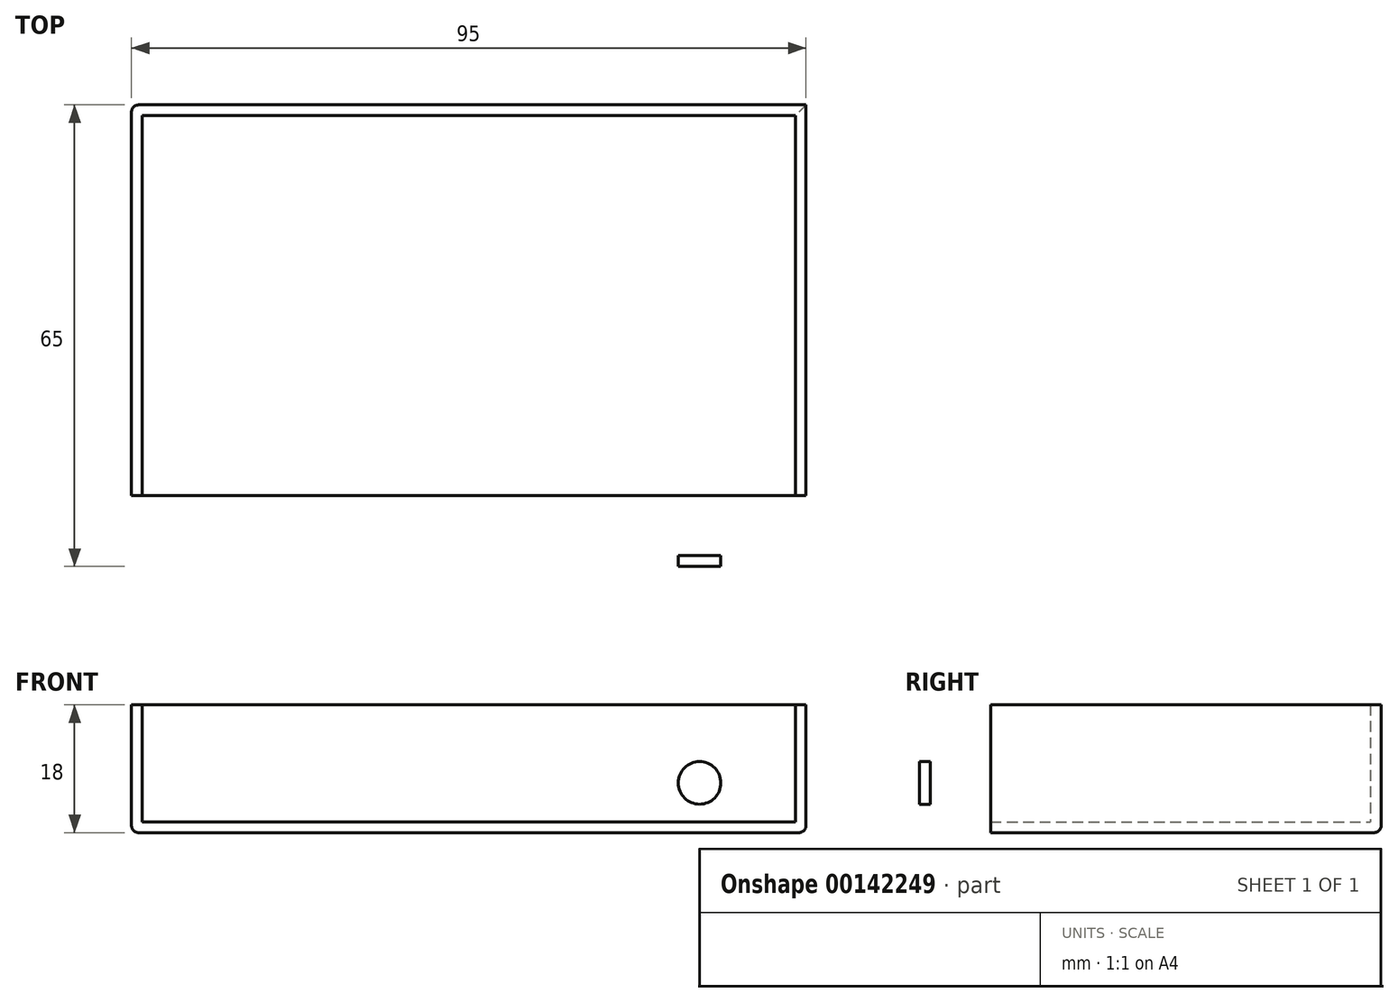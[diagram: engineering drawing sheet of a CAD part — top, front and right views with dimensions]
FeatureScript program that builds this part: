
annotation { "Feature Type Name" : "Feature", "Feature Type Description" : "" }
export const myFeature = defineFeature(function(context is Context, id is Id, definition is map)
    precondition{}
    {
        {
            var Q0;
            Q0=qCreatedBy(makeId("Top.planeOp"),FACE);
            var sketch = newSketch(context, id + "F0", { "sketchPlane" : qUnion([Q0])});
            skLineSegment(sketch, "E0.bottom", {"start": v(47.5, -32.5) * mm, "end": v(-47.5, -32.5) * mm});
            skLineSegment(sketch, "E0.top", {"start": v(47.5, 32.5) * mm, "end": v(-47.5, 32.5) * mm});
            skLineSegment(sketch, "E0.left", {"start": v(47.5, -32.5) * mm, "end": v(47.5, 32.5) * mm});
            skLineSegment(sketch, "E0.right", {"start": v(-47.5, -32.5) * mm, "end": v(-47.5, 32.5) * mm});
            skPoint(sketch, "E0.middle", {"position": v(0, 0) * mm});
            skSolve(sketch);
        }
        {
            var Q0;
            Q0 = qSketchRegion(id + "F0", true);
            extrude(context, id + "F1", {"entities" : qUnion([Q0]), "depth" : 18 * mm});
        }
        {
            var Q0;
            Q0=makeQuery(id+"F1.opExtrude","CAP_FACE",FACE,{"disambiguationData":[OSD([sQuery(id+"F0.wireOp",EDGE,"E0.bottom"),sQuery(id+"F0.wireOp",EDGE,"E0.top"),sQuery(id+"F0.wireOp",EDGE,"E0.left"),sQuery(id+"F0.wireOp",EDGE,"E0.right")])],"isStart":false});
            shell(context, id + "F2", {"entities" : qUnion([Q0]), "thickness" : 1.5 * mm});
        }
        {
            var Q0;
            Q0=makeQuery(id+"F1.opExtrude","SWEPT_FACE",FACE,{"disambiguationData":[OSD([sQuery(id+"F0.wireOp",EDGE,"E0.bottom")])]});
            var sketch = newSketch(context, id + "F3", { "sketchPlane" : qUnion([Q0])});
            skLineSegment(sketch, "E1", {"start": v(-32.5, 41.8) * mm, "end": v(-32.5, -33.12) * mm, "construction": true});
            skLineSegment(sketch, "E2", {"start": v(-65.73, 7) * mm, "end": v(14.2, 7) * mm, "construction": true});
            skCircle(sketch, "E3", {"center": v(-32.5, 7) * mm, "radius": 3 * mm});
            skCircle(sketch, "E4.MirrorC", {"center": v(32.5, 7) * mm, "radius": 3 * mm});
            skSolve(sketch);
        }
        {
            var Q0;
            Q0=makeQuery(id+"F3.imprint","IMPRINT",FACE,{"disambiguationData":[TD([[makeQuery(id+"F3.imprint","IMPRINT",EDGE,{"derivedFrom":sQuery(id+"F3.wireOp",EDGE,"E3")}),1.0]])]});
            var Q1;
            Q1=makeQuery(id+"F3.imprint","IMPRINT",FACE,{"disambiguationData":[TD([[makeQuery(id+"F3.imprint","IMPRINT",EDGE,{"derivedFrom":sQuery(id+"F3.wireOp",EDGE,"E4.MirrorC")}),-1.0]])]});
            extrude(context, id + "F4", {"entities" : qUnion([Q0, Q1]), "operationType" : NewBodyOperationType.REMOVE, "oppositeDirection" : true, "depth" : 10 * mm});
        }
        {
            var Q0;
            Q0=makeQuery(id+"F1.opExtrude","CAP_EDGE",EDGE,{"disambiguationData":[OSD([sQuery(id+"F0.wireOp",EDGE,"E0.left")])],"isStart":true});
            var Q1;
            Q1=makeQuery(id+"F1.opExtrude","CAP_EDGE",EDGE,{"disambiguationData":[OSD([sQuery(id+"F0.wireOp",EDGE,"E0.top")])],"isStart":true});
            var Q2;
            Q2=makeQuery(id+"F1.opExtrude","CAP_EDGE",EDGE,{"disambiguationData":[OSD([sQuery(id+"F0.wireOp",EDGE,"E0.bottom")])],"isStart":true});
            var Q3;
            Q3=makeQuery(id+"F1.opExtrude","CAP_EDGE",EDGE,{"disambiguationData":[OSD([sQuery(id+"F0.wireOp",EDGE,"E0.right")])],"isStart":true});
            var Q4;
            Q4=makeQuery(id+"F1.opExtrude","SWEPT_EDGE",EDGE,{"disambiguationData":[OSD([sQuery(id+"F0.wireOp",EDGE,"E0.bottom"),sQuery(id+"F0.wireOp",EDGE,"E0.right")])]});
            var Q5;
            Q5=makeQuery(id+"F1.opExtrude","SWEPT_EDGE",EDGE,{"disambiguationData":[OSD([sQuery(id+"F0.wireOp",EDGE,"E0.top"),sQuery(id+"F0.wireOp",EDGE,"E0.right")])]});
            fillet(context, id + "F5", {"entities" : qUnion([Q0, Q1, Q2, Q3, Q4, Q5]), "radius" : 1 * mm, "tangentPropagation" : true, "allowEdgeOverflow" : false});
        }
    });
